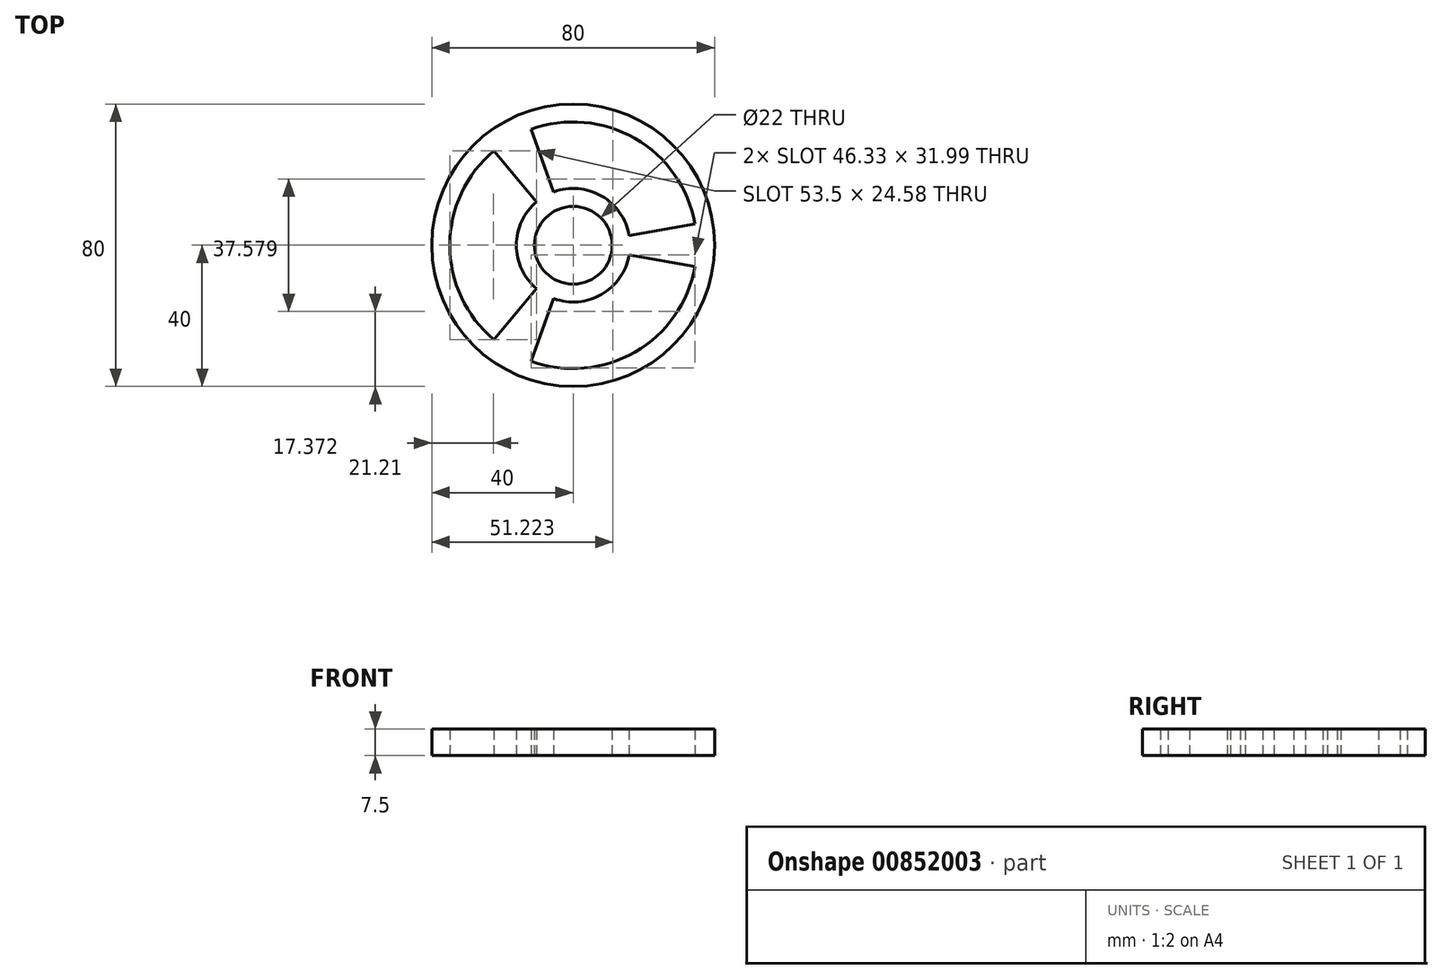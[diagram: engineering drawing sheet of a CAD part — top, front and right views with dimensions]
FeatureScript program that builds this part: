
annotation { "Feature Type Name" : "Feature", "Feature Type Description" : "" }
export const myFeature = defineFeature(function(context is Context, id is Id, definition is map)
    precondition{}
    {
        {
            var Q0;
            Q0=qCreatedBy(makeId("Top.planeOp"),FACE);
            var sketch = newSketch(context, id + "F0", { "sketchPlane" : qUnion([Q0])});
            skCircle(sketch, "E0", {"center": v(0, 0) * mm, "radius": 11 * mm});
            skCircle(sketch, "E1", {"center": v(0, 0) * mm, "radius": 16.08 * mm});
            skCircle(sketch, "E2", {"center": v(0, 0) * mm, "radius": 40 * mm});
            skCircle(sketch, "E3", {"center": v(0, 0) * mm, "radius": 34.92 * mm});
            skLineSegment(sketch, "E4", {"start": v(0, 0) * mm, "end": v(39.4, 6.95) * mm});
            skLineSegment(sketch, "E5.MirrorCS", {"start": v(0, 0) * mm, "end": v(39.4, -6.95) * mm});
            skLineSegment(sketch, "E6.1.0", {"start": v(0, 0) * mm, "end": v(-13.68, -37.59) * mm});
            skLineSegment(sketch, "E6.1.1", {"start": v(0, 0) * mm, "end": v(-25.71, -30.64) * mm});
            skLineSegment(sketch, "E6.2.0", {"start": v(0, 0) * mm, "end": v(-25.71, 30.64) * mm});
            skLineSegment(sketch, "E6.2.1", {"start": v(0, 0) * mm, "end": v(-13.68, 37.59) * mm});
            skLineSegment(sketch, "E6.anchor1", {"start": v(0, 0) * mm, "end": v(39.4, -6.95) * mm, "construction": true});
            skLineSegment(sketch, "E6.anchor2", {"start": v(0, 0) * mm, "end": v(-13.68, 37.59) * mm, "construction": true});
            skSolve(sketch);
        }
        {
            var Q0;
            {var subQ0=sQuery(id+"F0.wireOp",EDGE,"E6.2.0");var subQ1=sQuery(id+"F0.wireOp",EDGE,"E2");var subQ2=makeQuery(id+"F0.imprint","INTERSECT",VERTEX,{"derivedFrom":[subQ1,subQ0]});Q0=makeQuery(id+"F0.imprint","IMPRINT",FACE,{"disambiguationData":[TD([[makeQuery(id+"F0.imprint","IMPRINT",EDGE,{"disambiguationData":[TD([[subQ2,1.0]])],"derivedFrom":subQ1}),1.0]])]});}
            var Q1;
            {var subQ0=sQuery(id+"F0.wireOp",EDGE,"E6.1.1");var subQ1=sQuery(id+"F0.wireOp",EDGE,"E2");var subQ2=makeQuery(id+"F0.imprint","INTERSECT",VERTEX,{"derivedFrom":[subQ1,subQ0]});Q1=makeQuery(id+"F0.imprint","IMPRINT",FACE,{"disambiguationData":[TD([[makeQuery(id+"F0.imprint","IMPRINT",EDGE,{"disambiguationData":[TD([[subQ2,1.0]])],"derivedFrom":subQ1}),1.0]])]});}
            var Q2;
            {var subQ0=sQuery(id+"F0.wireOp",EDGE,"E4");var subQ1=sQuery(id+"F0.wireOp",EDGE,"E2");var subQ2=makeQuery(id+"F0.imprint","INTERSECT",VERTEX,{"derivedFrom":[subQ1,subQ0]});Q2=makeQuery(id+"F0.imprint","IMPRINT",FACE,{"disambiguationData":[TD([[makeQuery(id+"F0.imprint","IMPRINT",EDGE,{"disambiguationData":[TD([[subQ2,-1.0]])],"derivedFrom":subQ1}),1.0]])]});}
            var Q3;
            {var subQ0=sQuery(id+"F0.wireOp",EDGE,"E4");var subQ1=sQuery(id+"F0.wireOp",EDGE,"E2");var subQ2=makeQuery(id+"F0.imprint","INTERSECT",VERTEX,{"derivedFrom":[subQ1,subQ0]});Q3=makeQuery(id+"F0.imprint","IMPRINT",FACE,{"disambiguationData":[TD([[makeQuery(id+"F0.imprint","IMPRINT",EDGE,{"disambiguationData":[TD([[subQ2,1.0]])],"derivedFrom":subQ1}),1.0]])]});}
            var Q4;
            {var subQ0=sQuery(id+"F0.wireOp",EDGE,"E4");var subQ1=sQuery(id+"F0.wireOp",EDGE,"E1");var subQ2=makeQuery(id+"F0.imprint","INTERSECT",VERTEX,{"derivedFrom":[subQ1,subQ0]});Q4=makeQuery(id+"F0.imprint","IMPRINT",FACE,{"disambiguationData":[TD([[makeQuery(id+"F0.imprint","IMPRINT",EDGE,{"disambiguationData":[TD([[subQ2,1.0]])],"derivedFrom":subQ1}),-1.0]])]});}
            var Q5;
            {var subQ0=sQuery(id+"F0.wireOp",EDGE,"E4");var subQ1=sQuery(id+"F0.wireOp",EDGE,"E0");var subQ2=makeQuery(id+"F0.imprint","INTERSECT",VERTEX,{"derivedFrom":[subQ1,subQ0]});Q5=makeQuery(id+"F0.imprint","IMPRINT",FACE,{"disambiguationData":[TD([[makeQuery(id+"F0.imprint","IMPRINT",EDGE,{"disambiguationData":[TD([[subQ2,1.0]])],"derivedFrom":subQ1}),-1.0]])]});}
            var Q6;
            {var subQ0=sQuery(id+"F0.wireOp",EDGE,"E6.2.1");var subQ1=sQuery(id+"F0.wireOp",EDGE,"E0");var subQ2=makeQuery(id+"F0.imprint","INTERSECT",VERTEX,{"derivedFrom":[subQ1,subQ0]});Q6=makeQuery(id+"F0.imprint","IMPRINT",FACE,{"disambiguationData":[TD([[makeQuery(id+"F0.imprint","IMPRINT",EDGE,{"disambiguationData":[TD([[subQ2,1.0]])],"derivedFrom":subQ1}),-1.0]])]});}
            var Q7;
            {var subQ0=sQuery(id+"F0.wireOp",EDGE,"E6.2.1");var subQ1=sQuery(id+"F0.wireOp",EDGE,"E0");var subQ2=makeQuery(id+"F0.imprint","INTERSECT",VERTEX,{"derivedFrom":[subQ1,subQ0]});Q7=makeQuery(id+"F0.imprint","IMPRINT",FACE,{"disambiguationData":[TD([[makeQuery(id+"F0.imprint","IMPRINT",EDGE,{"disambiguationData":[TD([[subQ2,-1.0]])],"derivedFrom":subQ1}),-1.0]])]});}
            var Q8;
            {var subQ0=sQuery(id+"F0.wireOp",EDGE,"E6.2.1");var subQ1=sQuery(id+"F0.wireOp",EDGE,"E1");var subQ2=makeQuery(id+"F0.imprint","INTERSECT",VERTEX,{"derivedFrom":[subQ1,subQ0]});Q8=makeQuery(id+"F0.imprint","IMPRINT",FACE,{"disambiguationData":[TD([[makeQuery(id+"F0.imprint","IMPRINT",EDGE,{"disambiguationData":[TD([[subQ2,-1.0]])],"derivedFrom":subQ1}),-1.0]])]});}
            var Q9;
            {var subQ0=sQuery(id+"F0.wireOp",EDGE,"E6.2.0");var subQ1=sQuery(id+"F0.wireOp",EDGE,"E0");var subQ2=makeQuery(id+"F0.imprint","INTERSECT",VERTEX,{"derivedFrom":[subQ1,subQ0]});Q9=makeQuery(id+"F0.imprint","IMPRINT",FACE,{"disambiguationData":[TD([[makeQuery(id+"F0.imprint","IMPRINT",EDGE,{"disambiguationData":[TD([[subQ2,-1.0]])],"derivedFrom":subQ1}),-1.0]])]});}
            var Q10;
            {var subQ0=sQuery(id+"F0.wireOp",EDGE,"E6.1.1");var subQ1=sQuery(id+"F0.wireOp",EDGE,"E0");var subQ2=makeQuery(id+"F0.imprint","INTERSECT",VERTEX,{"derivedFrom":[subQ1,subQ0]});Q10=makeQuery(id+"F0.imprint","IMPRINT",FACE,{"disambiguationData":[TD([[makeQuery(id+"F0.imprint","IMPRINT",EDGE,{"disambiguationData":[TD([[subQ2,-1.0]])],"derivedFrom":subQ1}),-1.0]])]});}
            var Q11;
            {var subQ0=sQuery(id+"F0.wireOp",EDGE,"E6.1.0");var subQ1=sQuery(id+"F0.wireOp",EDGE,"E0");var subQ2=makeQuery(id+"F0.imprint","INTERSECT",VERTEX,{"derivedFrom":[subQ1,subQ0]});Q11=makeQuery(id+"F0.imprint","IMPRINT",FACE,{"disambiguationData":[TD([[makeQuery(id+"F0.imprint","IMPRINT",EDGE,{"disambiguationData":[TD([[subQ2,-1.0]])],"derivedFrom":subQ1}),-1.0]])]});}
            var Q12;
            {var subQ0=sQuery(id+"F0.wireOp",EDGE,"E6.1.1");var subQ1=sQuery(id+"F0.wireOp",EDGE,"E1");var subQ2=makeQuery(id+"F0.imprint","INTERSECT",VERTEX,{"derivedFrom":[subQ1,subQ0]});Q12=makeQuery(id+"F0.imprint","IMPRINT",FACE,{"disambiguationData":[TD([[makeQuery(id+"F0.imprint","IMPRINT",EDGE,{"disambiguationData":[TD([[subQ2,-1.0]])],"derivedFrom":subQ1}),-1.0]])]});}
            var Q13;
            {var subQ0=sQuery(id+"F0.wireOp",EDGE,"E6.1.0");var subQ1=sQuery(id+"F0.wireOp",EDGE,"E2");var subQ2=makeQuery(id+"F0.imprint","INTERSECT",VERTEX,{"derivedFrom":[subQ1,subQ0]});Q13=makeQuery(id+"F0.imprint","IMPRINT",FACE,{"disambiguationData":[TD([[makeQuery(id+"F0.imprint","IMPRINT",EDGE,{"disambiguationData":[TD([[subQ2,1.0]])],"derivedFrom":subQ1}),1.0]])]});}
            var Q14;
            {var subQ0=sQuery(id+"F0.wireOp",EDGE,"E5.MirrorCS");var subQ1=sQuery(id+"F0.wireOp",EDGE,"E2");var subQ2=makeQuery(id+"F0.imprint","INTERSECT",VERTEX,{"derivedFrom":[subQ1,subQ0]});Q14=makeQuery(id+"F0.imprint","IMPRINT",FACE,{"disambiguationData":[TD([[makeQuery(id+"F0.imprint","IMPRINT",EDGE,{"disambiguationData":[TD([[subQ2,1.0]])],"derivedFrom":subQ1}),1.0]])]});}
            extrude(context, id + "F1", {"entities" : qUnion([Q0, Q1, Q2, Q3, Q4, Q5, Q6, Q7, Q8, Q9, Q10, Q11, Q12, Q13, Q14]), "depth" : 7.5 * mm, "offsetDistance" : 25.4 * mm});
        }
    });
